# Revit family: ERA_LF_PR_SPP-404
name_source: partatom
category: Осветительные приборы
units: mm (PartAtom-declared; Revit-internal decimal feet)

## family parameters
Всегда вертикально = Да
Заголовок OmniClass = Lighting
Источник света = Да
На основе рабочей плоскости = Нет
Номер OmniClass = 23.80.70.00
Общий = Нет
При загрузке вырезать с полостями = Нет
Размер круглого соединителя = Использовать диаметр
Тип детали = Нормальный
Точка расчета площади = Да

## types (4) — shared parameters
ADSK_Единица измерения = шт.
ADSK_Завод-изготовитель = ЭРА
ADSK_Классификация нагрузок = Освещение
ADSK_Количество фаз = 1
ADSK_Коэффициент мощности = 0.95
ADSK_Наименование краткое = Светильник
ADSK_Напряжение = 230 В
ADSK_Примечание = Импульсный драйвер, поликарбонат
ADSK_Размер_Высота = 73 мм
ADSK_Размер_Ширина = 103 мм
URL = https://www.eraworld.ru
_Корпус_Высота = 73 мм
_Корпус_Диаметр = 1 мм
_Корпус_Ширина = 103 мм
_Подвес_Диаметр = 1 мм
_Подвес_Чаша_Высота = 20 мм
_Подвес_Чаша_Диаметр = 10 мм
_УГО_Ширина = 1.03 мм
Видимая форма излучения при визуализации = Нет
Высота чаши подвеса = 20 мм
Геометрия изделия = Прямоугольный
Диаметр подвеса = 1 мм
Диаметр чаши подвеса = 10 мм
Излучение по ширине прямоугольника = 103 мм
Источник света = LED
Класс защиты = I
Класс пожароопасности = Нет
Комплект = Импульсный драйвер
Разработчик модели = https://www.teslabim.ru
Светофильтр = 16777215
Смещение цветовой температуры при затухании лампы = <Нет>
Степень защиты IP = IP44
Тип установки = Подвесной
УГО_Масштаб = 100
Угол наклона = 90,00°
Файл фотометрической сетки = SPP-404-0-50K-050.ies
Цвет = Чёрный
zero-valued in all types: ADSK_Размер_Диаметр

## per-type parameters (varying)
| type | ADSK_Код изделия | ADSK_Марка | ADSK_Масса | ADSK_Наименование | ADSK_Номинальная мощность | ADSK_Обозначение | ADSK_Полная мощность | ADSK_Размер_Длина | _Корпус_Длина | _Подвес_Расстояние | _УГО_Диаметр | _УГО_Длина | Излучение по длине прямоугольника |
| SPP-404-0-50K-050, LED, IP44, 257х103х73 мм (ДхШхВ), 50 Вт, 5000 К, 5250 лм, класс защиты I, в комплекте (импульсный драйвер) | SPP-404-0-50K-050 | SPP-404-0-50K-050 | 1.06 | Светильник, LED, прямоугольный, подвесной, IP44, 257х103х73 мм (ДхШхВ), 50 Вт, 5000 К, 5250 лм, класс защиты I, в комплекте (импульсный драйвер) | 50 Вт | SPP-404-0-50K-050 | 53 В·А | 257 мм | 257 мм | 207 мм | 2.57 мм | 2.57 мм | 257 мм |
| SPP-404-0-50K-100, LED, IP44, 502х103х73 мм (ДхШхВ), 100 Вт, 5000 К, 10500 лм, класс защиты I, в комплекте (импульсный драйвер) | SPP-404-0-50K-100 | SPP-404-0-50K-100 | 1.96 | Светильник, LED, прямоугольный, подвесной, IP44, 502х103х73 мм (ДхШхВ), 100 Вт, 5000 К, 10500 лм, класс защиты I, в комплекте (импульсный драйвер) | 100 Вт | SPP-404-0-50K-100 | 105 В·А | 502 мм | 502 мм | 452 мм | 5.02 мм | 5.02 мм | 502 мм |
| SPP-404-0-50K-150, LED, IP44, 747х103х73 мм (ДхШхВ), 150 Вт, 5000 К, 15750 лм, класс защиты I, в комплекте (импульсный драйвер) | SPP-404-0-50K-150 | SPP-404-0-50K-150 | 2.84 | Светильник, LED, прямоугольный, подвесной, IP44, 747х103х73 мм (ДхШхВ), 150 Вт, 5000 К, 15750 лм, класс защиты I, в комплекте (импульсный драйвер) | 150 Вт | SPP-404-0-50K-150 | 158 В·А | 747 мм | 747 мм | 697 мм | 7.47 мм | 7.47 мм | 747 мм |
| SPP-404-0-50K-200, LED, IP44, 992х103х73 мм (ДхШхВ), 200 Вт, 5000 К, 21000 лм, класс защиты I, в комплекте (импульсный драйвер) | SPP-404-0-50K-200 | SPP-404-0-50K-200 | 3.72 | Светильник, LED, прямоугольный, подвесной, IP44, 992х103х73 мм (ДхШхВ), 200 Вт, 5000 К, 21000 лм, класс защиты I, в комплекте (импульсный драйвер) | 200 Вт | SPP-404-0-50K-200 | 211 В·А | 992 мм | 992 мм | 942 мм | 9.92 мм | 9.92 мм | 992 мм |
